# Revit family: PAL
name_source: partatom
category: Specialty Equipment
revit_build: Autodesk Revit Architecture 2015 (Build: 20141119_1515(x64)
units: mm (PartAtom-declared; Revit-internal decimal feet)

## types (18) — shared parameters
Capacity = 30-50k
Curb = 0' - 3"
Description = Power Assist Leveler
LipLength = 1' - 6"
Manufacturer = Serco Entrematic
Model = PAL
URL = http://sercoentrematic.com

## per-type parameters (varying)
| type | LipExtension | PitDepth | PitDepthR | PitLength | PitWidth |
| 6 | 0' - 0" | 1' - 8" | 1' - 7 1/2" | 5' - 3" | 6' - 1" |
| 86 | 0' - 0" | 1' - 8" | 1' - 7 1/2" | 7' - 3" | 6' - 1" |
| 66.5 | 0' - 0" | 1' - 8" | 1' - 7 1/2" | 5' - 3" | 6' - 7" |
| 86.5 | 0' - 0" | 1' - 8" | 1' - 7 1/2" | 7' - 3" | 6' - 7" |
| 67 | 0' - 0" | 1' - 8" | 1' - 7 1/2" | 5' - 3" | 7' - 1" |
| 87 | 0' - 0" | 1' - 8" | 1' - 7 1/2" | 7' - 3" | 7' - 1" |
| 106 | 0' - 0" | 2' - 0" | 1' - 11 1/2" | 9' - 3" | 6' - 1" |
| 106.5 | 0' - 0" | 2' - 0" | 1' - 11 1/2" | 9' - 3" | 6' - 7" |
| 107 | 0' - 0" | 2' - 0" | 1' - 11 1/2" | 9' - 3" | 7' - 1" |
| 106 Barrier Lip | 0' - 5" | 2' - 0" | 1' - 11 1/2" | 9' - 3" | 6' - 1" |
| 106.5 Barrier Lip | 0' - 5" | 2' - 0" | 1' - 11 1/2" | 9' - 3" | 6' - 7" |
| 107 Barrier Lip | 0' - 5" | 2' - 0" | 1' - 11 1/2" | 9' - 3" | 7' - 1" |
| 6 Barrier Lip | 0' - 5" | 1' - 8" | 1' - 7 1/2" | 5' - 3" | 6' - 1" |
| 66.5 Barrier Lip | 0' - 5" | 1' - 8" | 1' - 7 1/2" | 5' - 3" | 6' - 7" |
| 67 Barrier Lip | 0' - 5" | 1' - 8" | 1' - 7 1/2" | 5' - 3" | 7' - 1" |
| 86 Barrier Lip | 0' - 5" | 1' - 8" | 1' - 7 1/2" | 7' - 3" | 6' - 1" |
| 86.5 Barrier Lip | 0' - 5" | 1' - 8" | 1' - 7 1/2" | 7' - 3" | 6' - 7" |
| 87 Barrier Lip | 0' - 5" | 1' - 8" | 1' - 7 1/2" | 7' - 3" | 7' - 1" |

## geometry (parser evidence)
native form markers: Blend x2, Sweep x3
no freeform markers — native parametric forms only
